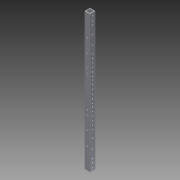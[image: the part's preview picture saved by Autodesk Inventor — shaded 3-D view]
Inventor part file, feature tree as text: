
AUTODESK INVENTOR PART (.ipt)
format: ipt  version: 2013 (Build 170138000, 138)  size: 232,448 bytes
history: native  units: in
note: dims shown in document units (in); Inventor stores cm internally (conversion verified against a paired STEP export)
features: reference x7, extrude x4, sketch x4
ambient origin geometry x8: Origin, YZ Plane, XZ Plane, XY Plane, X Axis, Y Axis, Z Axis, Center Point
bodies: Solid1 (feature_tree)
feature tree (15):
  extrude  "Extrusion1"  Depth=1.0in
  extrude  "Extrusion2"  Depth=26.0in TaperAngle=0.0deg
  extrude  "Extrusion3"  Depth=1.75in
  extrude  "Extrusion4"  Depth=1.75in
  sketch  "Sketch1"  dims[d0=1.0in d1=1.0in]
  sketch  "Sketch2"  dims[d2=0.125in d3=26.0in d4=0.0in]
  sketch  "Sketch3"  dims[d5=1.0in d6=0.0in d7=1.75in]
  reference  "Reference11"
  reference  "Reference12"
  reference  "Reference13"
  sketch  "Sketch4"  dims[d8=2.375in d9=1.75in d10=1.75in d11=0.26in d12=0.26in d13=0.26in d14=0.26in d15=0.26in d16=0.26in d17=0.26in d18=0.26in d19=1.0in d20=0.0in d21=2.375in d22=0.26in d23=0.26in d27=0.375in d28=0.375in d33=3.5in d34=0.26in d35=2.7559in d37=0.75in d38=0.3937in d40=1.0in d42=2.7559in d44=0.75in d45=0.3937in d47=1.0in d49=1.0in d50=0.0in d51=0.75in d52=0.75in d53=0.75in d54=0.75in]
  reference  "Reference15"
  reference  "Reference16"
  reference  "Reference17"
  reference  "Reference18"
